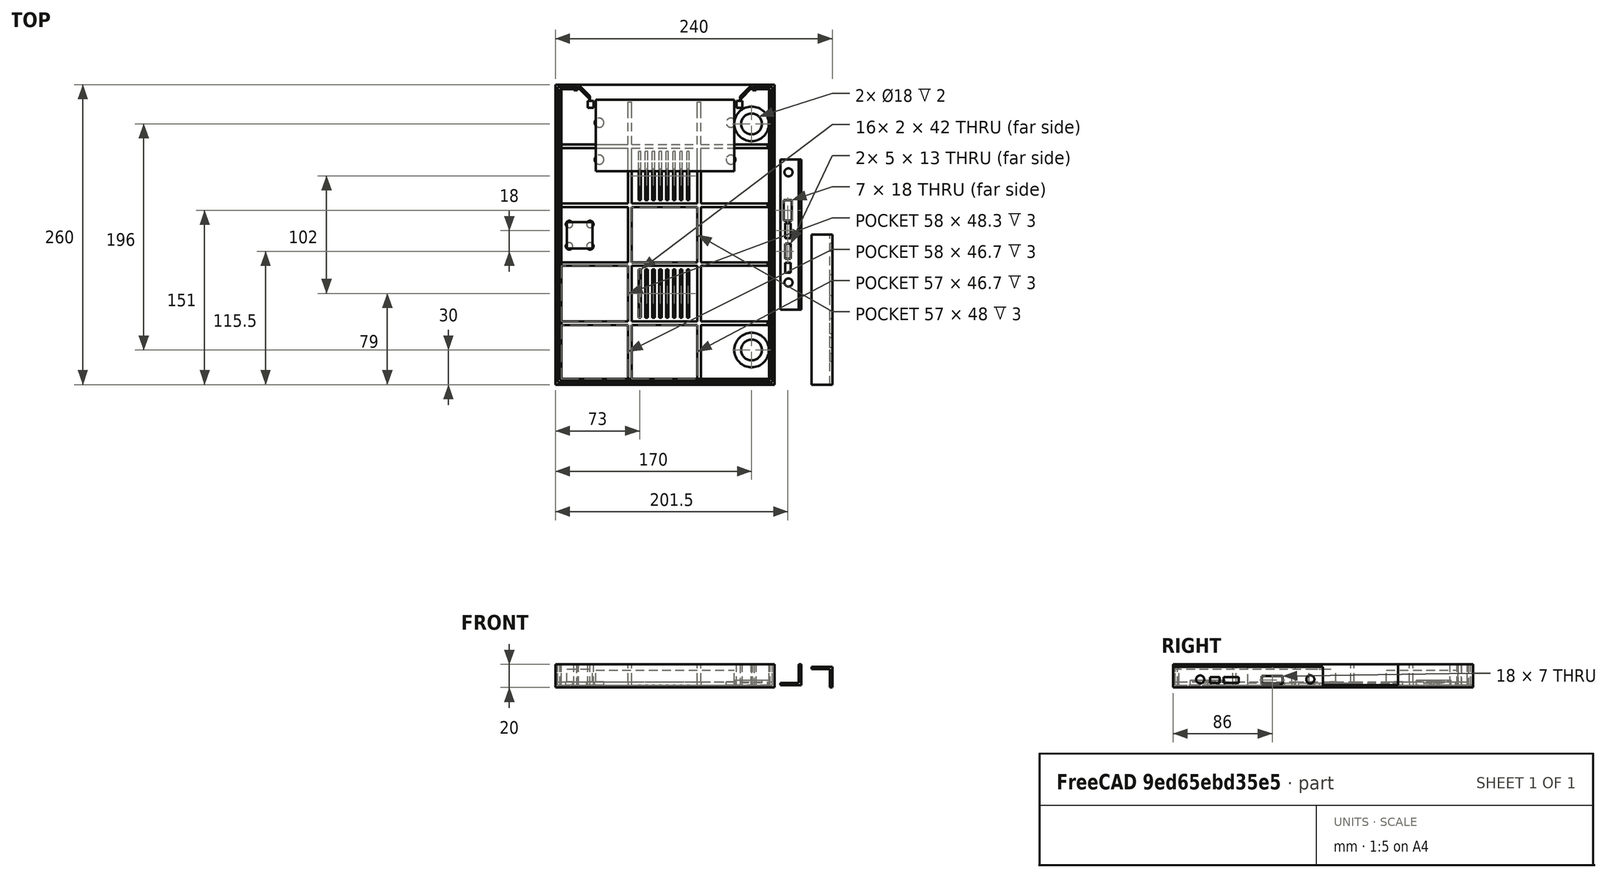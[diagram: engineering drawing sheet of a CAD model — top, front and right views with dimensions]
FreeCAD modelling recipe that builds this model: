
FCSTD DOCUMENT  (FreeCAD 0.16R6706 (Git))
Label: tapadero de conectores copia 2
License: All rights reserved
LicenseURL: http://en.wikipedia.org/wiki/All_rights_reserved
objects: Part::Box×60, Part::MultiFuse×16, Part::Cylinder×14, Part::Cut×11, Part::Fillet×1
note: 102 computed .brp shape members not serialized (recipe doc carries the construction recipe); baked Part::Feature solids carry a one-line shape summary decoded from their .brp

FEATURE [Part::Box] Box  label="tapadero de conectores"
  Height = 2
  Length = 18
  Width = 130
FEATURE [Part::Cylinder] Cylinder  label="taladro dc in"
  Angle = 360
  Height = 25
  Placement = pos=(7,23.5,0) rot=(0,0,1;0rad)
  Radius = 3.5
FEATURE [Part::Cylinder] Cylinder001  label="taladro headphone"
  Angle = 360
  Height = 25
  Placement = pos=(7,119,0) rot=(0,0,1;0rad)
  Radius = 3.5
FEATURE [Part::Box] Box001  label="hdmi 1"
  Height = 25
  Length = 7
  Placement = pos=(3,77,0) rot=(0,0,1;0rad)
  Width = 18
FEATURE [Part::Box] Box002  label="mini hdmi 1"
  Height = 25
  Length = 5
  Placement = pos=(4,44,0) rot=(0,0,1;0rad)
  Width = 13
FEATURE [Part::Box] Box003  label="micro usb"
  Height = 25
  Length = 5
  Placement = pos=(4,32,0) rot=(0,0,1;0rad)
  Width = 8.5
FEATURE [Part::MultiFuse] Fusion
  Placement = pos=(0,0,-2) rot=(0,0,1;0rad)
  Shapes = -> [Cylinder,Cylinder001,Box001,Box002,Box003]
FEATURE [Part::Cut] Cut  label="la tapa de conectores cortada"
  Base = -> Box
  Tool = -> Fusion
FEATURE [Part::Box] Box004  label="Cube"
  Height = 18
  Length = 2
  Placement = pos=(16,0,0) rot=(0,0,1;0rad)
  Width = 130
FEATURE [Part::MultiFuse] Fusion001  label="la tapa de conectores terminada"
  Placement = pos=(240,0,0) rot=(0,-1,0;1.5708rad)
  Shapes = -> [Cut,Box004]
FEATURE [Part::Box] Box005  label="base fuera"
  Height = 20
  Length = 190
  Width = 260
FEATURE [Part::Box] Box006  label="base dentro"
  Height = 18
  Length = 186
  Placement = pos=(2,2,2) rot=(0,0,1;0rad)
  Width = 256
FEATURE [Part::Cut] Cut001  label="base vacio"
  Base = -> Box005
  Tool = -> Box006
FEATURE [Part::Box] Box007  label="cortador derecho"
  Height = 25
  Length = 150
  Placement = pos=(20,245,2) rot=(0,0,1;0rad)
  Width = 30
FEATURE [Part::Cut] Cut002  label="base cortado"
  Base = -> Cut001
  Tool = -> Box007
FEATURE [Part::Box] Box008  label="orilla 1"
  Height = 18
  Length = 2
  Placement = pos=(20,260,2) rot=(0,0,1;3.92699rad)
  Width = 17
FEATURE [Part::Box] Box009  label="orilla 002"
  Height = 18
  Length = 2
  Placement = pos=(171,258,2) rot=(0,0,1;2.35619rad)
  Width = 16
FEATURE [Part::MultiFuse] Fusion002  label="la base"
  Shapes = -> [Cut002,Box008,Box009]
FEATURE [Part::Box] Box010  label="mini hdmi 002"
  Height = 25
  Length = 5
  Placement = pos=(4,62,0) rot=(0,0,1;0rad)
  Width = 13
FEATURE [Part::MultiFuse] Fusion003
  Shapes = -> [Cylinder,Cylinder001,Box001,Box002,Box003,Box010]
FEATURE [Part::Cut] Cut003
  Base = -> Box
  Tool = -> Fusion003
FEATURE [Part::MultiFuse] Fusion004  label="la tapa final"
  Placement = pos=(195,65,2) rot=(0,0,1;0rad)
  Shapes = -> [Cut003,Box004]
FEATURE [Part::Box] Box011  label="cortador de orillas"
  Height = 25
  Length = 130
  Placement = pos=(30,235,2) rot=(0,0,1;0rad)
  Width = 30
FEATURE [Part::MultiFuse] Fusion005  label="la base con orillas"
  Shapes = -> [Fusion002,Box008,Box009]
FEATURE [Part::Cut] Cut004
  Base = -> Fusion005
  Tool = -> Box011
FEATURE [Part::Cut] Cut005
  Base = -> Fusion005
  Tool = -> Box011
FEATURE [Part::Fillet] Fillet  label="la carcasa redondeada"
  Base = -> Cut005
  Edges = 4 edges r=2: [Edge1,Edge3,Edge6,Edge20]
FEATURE [Part::Box] Box012  label="base fuera001"
  Height = 18
  Length = 186
  Placement = pos=(2,2,2) rot=(0,0,1;0rad)
  Width = 256
FEATURE [Part::Box] Box013  label="base dentro001"
  Height = 20
  Length = 182
  Placement = pos=(4,4,2) rot=(0,0,1;0rad)
  Width = 252
FEATURE [Part::Cut] Cut006  label="base vacio001"
  Base = -> Box012
  Tool = -> Box013
FEATURE [Part::Box] Box014  label="cortador derecho001"
  Height = 25
  Length = 154
  Placement = pos=(18,241,2) rot=(0,0,1;0rad)
  Width = 30
FEATURE [Part::Cut] Cut007  label="refuerzo base"
  Base = -> Cut006
  Tool = -> Box014
FEATURE [Part::Box] Box015  label="refuerzo1"
  Height = 18
  Length = 3
  Placement = pos=(2,2,2) rot=(0,0,1;0rad)
  Width = 3
FEATURE [Part::Box] Box016  label="refuerzo2"
  Height = 18
  Length = 3
  Placement = pos=(2,51.7,2) rot=(0,0,1;0rad)
  Width = 3
FEATURE [Part::Box] Box017  label="refuerzo3"
  Height = 18
  Length = 3
  Placement = pos=(2,103,2) rot=(0,0,1;0rad)
  Width = 3
FEATURE [Part::Box] Box018  label="refuerzo4"
  Height = 18
  Length = 3
  Placement = pos=(2,154,2) rot=(0,0,1;0rad)
  Width = 3
FEATURE [Part::Box] Box019  label="refuerzo5"
  Height = 18
  Length = 3
  Placement = pos=(2,205,2) rot=(0,0,1;0rad)
  Width = 3
FEATURE [Part::Box] Box020  label="refuerzo6"
  Height = 18
  Length = 3
  Placement = pos=(2,255,2) rot=(0,0,1;0rad)
  Width = 3
FEATURE [Part::Box] Box021  label="refuerzo7"
  Height = 3
  Length = 3
  Placement = pos=(2,2,2) rot=(0,0,1;0rad)
  Width = 254
FEATURE [Part::MultiFuse] Fusion006  label="refuerzo superior"
  Shapes = -> [Box015,Box016,Box017,Box018,Box019,Box020,Box021]
FEATURE [Part::Box] Box022  label="refuerzo008"
  Height = 18
  Length = 3
  Placement = pos=(2,2,2) rot=(0,0,1;0rad)
  Width = 3
FEATURE [Part::Box] Box023  label="refuerzo009"
  Height = 18
  Length = 3
  Placement = pos=(2,51.7,2) rot=(0,0,1;0rad)
  Width = 3
FEATURE [Part::Box] Box024  label="refuerzo010"
  Height = 18
  Length = 3
  Placement = pos=(2,103,2) rot=(0,0,1;0rad)
  Width = 3
FEATURE [Part::Box] Box025  label="refuerzo011"
  Height = 18
  Length = 3
  Placement = pos=(2,154,2) rot=(0,0,1;0rad)
  Width = 3
FEATURE [Part::Box] Box026  label="refuerzo012"
  Height = 18
  Length = 3
  Placement = pos=(2,205,2) rot=(0,0,1;0rad)
  Width = 3
FEATURE [Part::Box] Box027  label="refuerzo013"
  Height = 18
  Length = 3
  Placement = pos=(2,255,2) rot=(0,0,1;0rad)
  Width = 3
FEATURE [Part::Box] Box028  label="refuerzo014"
  Height = 3
  Length = 3
  Placement = pos=(2,2,2) rot=(0,0,1;0rad)
  Width = 254
FEATURE [Part::MultiFuse] Fusion007  label="refuerzo interior"
  Placement = pos=(183,0,0) rot=(0,0,1;0rad)
  Shapes = -> [Box022,Box023,Box024,Box025,Box026,Box027,Box028]
FEATURE [Part::Box] Box029  label="refuerzo izq"
  Height = 18
  Length = 3
  Placement = pos=(63,2,2) rot=(0,0,1;0rad)
  Width = 3
FEATURE [Part::Box] Box030  label="refuerzo izq2"
  Height = 18
  Length = 3
  Placement = pos=(123,2,2) rot=(0,0,1;0rad)
  Width = 3
FEATURE [Part::Box] Box031  label="ref izq larg"
  Height = 3
  Length = 182
  Placement = pos=(2,2,2) rot=(0,0,1;0rad)
  Width = 3
FEATURE [Part::Box] Box032  label="ref izq larg001"
  Height = 3
  Length = 182
  Placement = pos=(2,51.7,2) rot=(0,0,1;0rad)
  Width = 3
FEATURE [Part::Box] Box033  label="ref izq larg002"
  Height = 3
  Length = 182
  Placement = pos=(2,103,2) rot=(0,0,1;0rad)
  Width = 3
FEATURE [Part::Box] Box034  label="ref izq larg003"
  Height = 3
  Length = 182
  Placement = pos=(2,154,2) rot=(0,0,1;0rad)
  Width = 3
FEATURE [Part::Box] Box035  label="ref izq larg004"
  Height = 3
  Length = 182
  Placement = pos=(2,205,2) rot=(0,0,1;0rad)
  Width = 3
FEATURE [Part::Box] Box036  label="ref sup 2"
  Height = 3
  Length = 3
  Placement = pos=(63,2,2) rot=(0,0,1;0rad)
  Width = 243
FEATURE [Part::Box] Box037  label="ref sup 3"
  Height = 3
  Length = 3
  Placement = pos=(123,2,2) rot=(0,0,1;0rad)
  Width = 243
FEATURE [Part::Box] Box038  label="ref orilla1"
  Height = 18
  Length = 3
  Placement = pos=(16,255,2) rot=(0,0,1;0rad)
  Width = 3
FEATURE [Part::Box] Box039  label="ref orilla2"
  Height = 18
  Length = 3
  Placement = pos=(171,255,2) rot=(0,0,1;0rad)
  Width = 3
FEATURE [Part::MultiFuse] Fusion008  label="el refuerzo"
  Shapes = -> [Fusion006,Fusion007,Box029,Box030,Box031,Box032,Box033,Box034,Box035,Box036,Box037,Box038,Box039]
FEATURE [Part::Box] Box040  label="controlador"
  Height = 10
  Length = 120
  Placement = pos=(35,185,5) rot=(0,0,1;0rad)
  Width = 62
FEATURE [Part::Box] Box041  label="tornillo1 tapa"
  Height = 18
  Length = 5
  Placement = pos=(28,240,2) rot=(0,0,1;0rad)
  Width = 6
FEATURE [Part::Box] Box042  label="tornillo2 tapa"
  Height = 18
  Length = 5
  Placement = pos=(157,240,2) rot=(0,0,1;0rad)
  Width = 6
FEATURE [Part::Cylinder] Cylinder002  label="tornillo control1"
  Angle = 360
  Height = 3
  Placement = pos=(152,195,2) rot=(0,0,1;0rad)
  Radius = 4
FEATURE [Part::Cylinder] Cylinder003  label="tornillo control2"
  Angle = 360
  Height = 3
  Placement = pos=(38,195,2) rot=(0,0,1;0rad)
  Radius = 4
FEATURE [Part::Cylinder] Cylinder004  label="tornillo control3"
  Angle = 360
  Height = 3
  Placement = pos=(152,227,2) rot=(0,0,1;0rad)
  Radius = 4
FEATURE [Part::Cylinder] Cylinder005  label="tornillo control004"
  Angle = 360
  Height = 3
  Placement = pos=(38,227,2) rot=(0,0,1;0rad)
  Radius = 4
FEATURE [Part::MultiFuse] Fusion009  label="los tornillos controlador"
  Shapes = -> [Box041,Box042,Cylinder002,Cylinder003,Cylinder004,Cylinder005]
FEATURE [Part::Cylinder] Cylinder006  label="Cylinder"
  Angle = 360
  Height = 6
  Placement = pos=(0,0,4) rot=(0,0,1;0rad)
  Radius = 9
FEATURE [Part::Cylinder] Cylinder007  label="Cylinder001"
  Angle = 360
  Height = 4
  Placement = pos=(0,0,2) rot=(0,0,1;0rad)
  Radius = 15
FEATURE [Part::Cut] Cut008  label="altavoz derecho"
  Base = -> Cylinder007
  Placement = pos=(170,226,0) rot=(0,0,1;0rad)
  Tool = -> Cylinder006
FEATURE [Part::Cylinder] Cylinder008  label="Cylinder010"
  Angle = 360
  Height = 6
  Placement = pos=(0,0,4) rot=(0,0,1;0rad)
  Radius = 9
FEATURE [Part::Cylinder] Cylinder009  label="Cylinder011"
  Angle = 360
  Height = 4
  Placement = pos=(0,0,2) rot=(0,0,1;0rad)
  Radius = 15
FEATURE [Part::Cut] Cut009  label="altavoz izquierdo"
  Base = -> Cylinder009
  Placement = pos=(170,30,0) rot=(0,0,1;0rad)
  Tool = -> Cylinder008
FEATURE [Part::MultiFuse] Fusion010  label="los altavoces"
  Shapes = -> [Cut008,Cut009]
FEATURE [Part::Box] Box043  label="ventil1"
  Height = 26
  Length = 2
  Placement = pos=(72,58,-2) rot=(0,0,1;0rad)
  Width = 42
FEATURE [Part::Box] Box044  label="ventil002"
  Height = 26
  Length = 2
  Placement = pos=(78,58,-2) rot=(0,0,1;0rad)
  Width = 42
FEATURE [Part::Box] Box045  label="ventil003"
  Height = 26
  Length = 2
  Placement = pos=(84,58,-2) rot=(0,0,1;0rad)
  Width = 42
FEATURE [Part::Box] Box046  label="ventil004"
  Height = 26
  Length = 2
  Placement = pos=(90,58,-2) rot=(0,0,1;0rad)
  Width = 42
FEATURE [Part::Box] Box047  label="ventil005"
  Height = 26
  Length = 2
  Placement = pos=(96,58,-2) rot=(0,0,1;0rad)
  Width = 42
FEATURE [Part::Box] Box048  label="ventil006"
  Height = 26
  Length = 2
  Placement = pos=(102,58,-2) rot=(0,0,1;0rad)
  Width = 42
FEATURE [Part::Box] Box049  label="ventil007"
  Height = 26
  Length = 2
  Placement = pos=(108,58,-2) rot=(0,0,1;0rad)
  Width = 42
FEATURE [Part::Box] Box050  label="ventil008"
  Height = 26
  Length = 2
  Placement = pos=(114,58,-2) rot=(0,0,1;0rad)
  Width = 42
FEATURE [Part::MultiFuse] Fusion011  label="ventilacion izq"
  Shapes = -> [Box043,Box044,Box045,Box046,Box047,Box048,Box049,Box050]
FEATURE [Part::Box] Box051  label="ventil009"
  Height = 26
  Length = 2
  Placement = pos=(72,58,-2) rot=(0,0,1;0rad)
  Width = 42
FEATURE [Part::Box] Box052  label="ventil010"
  Height = 26
  Length = 2
  Placement = pos=(78,58,-2) rot=(0,0,1;0rad)
  Width = 42
FEATURE [Part::Box] Box053  label="ventil011"
  Height = 26
  Length = 2
  Placement = pos=(84,58,-2) rot=(0,0,1;0rad)
  Width = 42
FEATURE [Part::Box] Box054  label="ventil012"
  Height = 26
  Length = 2
  Placement = pos=(90,58,-2) rot=(0,0,1;0rad)
  Width = 42
FEATURE [Part::Box] Box055  label="ventil013"
  Height = 26
  Length = 2
  Placement = pos=(96,58,-2) rot=(0,0,1;0rad)
  Width = 42
FEATURE [Part::Box] Box056  label="ventil014"
  Height = 26
  Length = 2
  Placement = pos=(102,58,-2) rot=(0,0,1;0rad)
  Width = 42
FEATURE [Part::Box] Box057  label="ventil015"
  Height = 26
  Length = 2
  Placement = pos=(108,58,-2) rot=(0,0,1;0rad)
  Width = 42
FEATURE [Part::Box] Box058  label="ventil016"
  Height = 26
  Length = 2
  Placement = pos=(114,58,-2) rot=(0,0,1;0rad)
  Width = 42
FEATURE [Part::MultiFuse] Fusion012  label="ventilacion derech"
  Placement = pos=(0,102,0) rot=(0,0,1;0rad)
  Shapes = -> [Box051,Box052,Box053,Box054,Box055,Box056,Box057,Box058]
FEATURE [Part::MultiFuse] Fusion013  label="ventilacion"
  Shapes = -> [Fusion011,Fusion012]
FEATURE [Part::Cut] Cut010  label="la ventilacion"
  Base = -> Fillet
  Tool = -> Fusion013
FEATURE [Part::Box] Box059  label="amp1"
  Height = 11
  Length = 22
  Placement = pos=(10,118,5) rot=(0,0,1;0rad)
  Width = 23
FEATURE [Part::Cylinder] Cylinder010  label="torn1 amp"
  Angle = 360
  Height = 3
  Placement = pos=(2,2,2) rot=(0,0,1;0rad)
  Radius = 3
FEATURE [Part::Cylinder] Cylinder011  label="torn2 amp"
  Angle = 360
  Height = 3
  Placement = pos=(2,21,2) rot=(0,0,1;0rad)
  Radius = 3
FEATURE [Part::Cylinder] Cylinder012  label="torn3 amp"
  Angle = 360
  Height = 3
  Placement = pos=(20,2,2) rot=(0,0,1;0rad)
  Radius = 3
FEATURE [Part::Cylinder] Cylinder013  label="torn4 amp"
  Angle = 360
  Height = 3
  Placement = pos=(20,21,2) rot=(0,0,1;0rad)
  Radius = 3
FEATURE [Part::MultiFuse] Fusion014
  Placement = pos=(10,118,0) rot=(0,0,1;0rad)
  Shapes = -> [Cylinder010,Cylinder011,Cylinder012,Cylinder013]
FEATURE [Part::MultiFuse] Fusion015  label="la pieza"
  Shapes = -> [Fusion004,Fusion008,Fusion009,Fusion010,Cut010,Fusion014]
